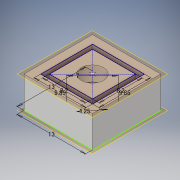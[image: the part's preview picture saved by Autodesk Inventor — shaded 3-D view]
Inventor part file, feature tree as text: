
AUTODESK INVENTOR PART (.ipt)
format: ipt  version: 2019 (Build 230136000, 136)  size: 135,168 bytes
history: native  units: in
note: dims shown in document units (in); Inventor stores cm internally (conversion verified against a paired STEP export)
features: extrude x4, sketch x2, other x1
ambient origin geometry x8: Origin, YZ Plane, XZ Plane, XY Plane, X Axis, Y Axis, Z Axis, Center Point
bodies: Body1 (feature_tree)
feature tree (7):
  other  "作業平面2"
  sketch  "スケッチ3"
  sketch  "スケッチ1"
  extrude  "押し出し8"  Depth=0.2362in
  extrude  "押し出し9"  Depth=0.3228in
  extrude  "押し出し10"  Depth=0.3228in
  extrude  "押し出し11"  Depth=0.3878in
